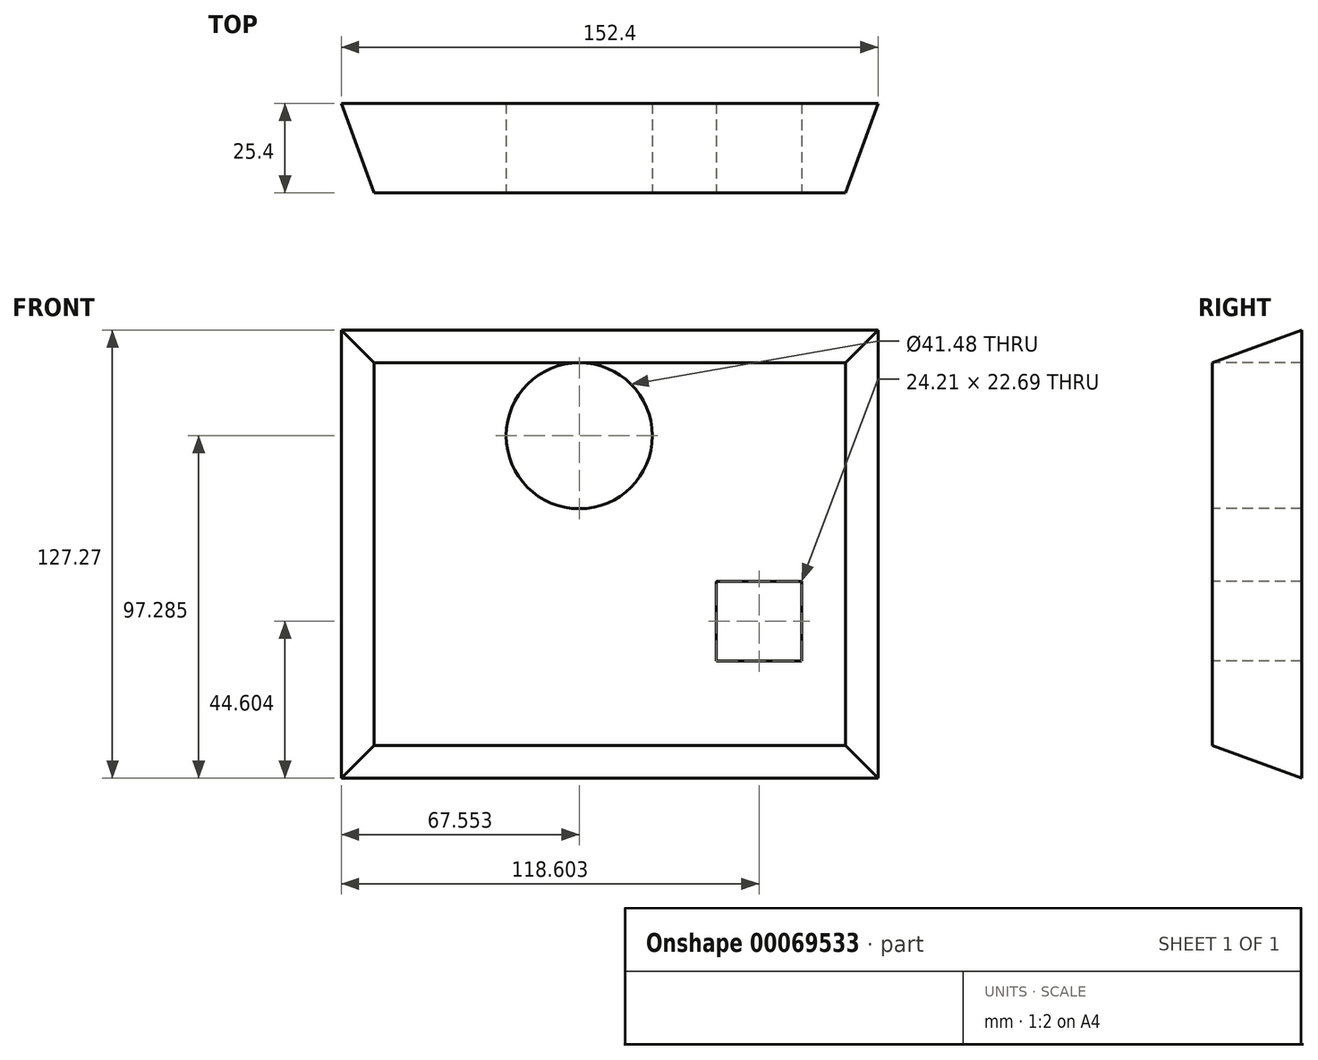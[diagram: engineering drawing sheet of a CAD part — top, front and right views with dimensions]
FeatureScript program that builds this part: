
annotation { "Feature Type Name" : "Feature", "Feature Type Description" : "" }
export const myFeature = defineFeature(function(context is Context, id is Id, definition is map)
    precondition{}
    {
        {
            var Q0;
            Q0=qCreatedBy(makeId("Front.planeOp"),FACE);
            var sketch = newSketch(context, id + "F0", { "sketchPlane" : qUnion([Q0])});
            skLineSegment(sketch, "E0.bottom", {"start": v(0, 0) * mm, "end": v(152.4, 0) * mm});
            skLineSegment(sketch, "E0.top", {"start": v(0, 127.27) * mm, "end": v(152.4, 127.27) * mm});
            skLineSegment(sketch, "E0.left", {"start": v(0, 0) * mm, "end": v(0, 127.27) * mm});
            skLineSegment(sketch, "E0.right", {"start": v(152.4, 0) * mm, "end": v(152.4, 127.27) * mm});
            skSolve(sketch);
        }
        {
            var Q0;
            Q0 = qSketchRegion(id + "F0", true);
            extrude(context, id + "F1", {"entities" : qUnion([Q0]), "depth" : 25.4 * mm, "hasDraft" : true, "draftAngle" : 20 * degree, "draftPullDirection" : true});
        }
        {
            var Q0;
            Q0=makeQuery(id+"F1.opExtrude","CAP_FACE",FACE,{"disambiguationData":[OSD([sQuery(id+"F0.wireOp",EDGE,"E0.bottom"),sQuery(id+"F0.wireOp",EDGE,"E0.top"),sQuery(id+"F0.wireOp",EDGE,"E0.left"),sQuery(id+"F0.wireOp",EDGE,"E0.right")])],"isStart":false});
            var sketch = newSketch(context, id + "F2", { "sketchPlane" : qUnion([Q0])});
            skLineSegment(sketch, "E1.bottom", {"start": v(130.7, 33.26) * mm, "end": v(106.5, 33.26) * mm});
            skLineSegment(sketch, "E1.top", {"start": v(130.7, 55.95) * mm, "end": v(106.5, 55.95) * mm});
            skLineSegment(sketch, "E1.left", {"start": v(130.7, 33.26) * mm, "end": v(130.7, 55.95) * mm});
            skLineSegment(sketch, "E1.right", {"start": v(106.5, 33.26) * mm, "end": v(106.5, 55.95) * mm});
            skSolve(sketch);
        }
        {
            var Q0;
            Q0 = qSketchRegion(id + "F2", true);
            extrude(context, id + "F3", {"entities" : qUnion([Q0]), "operationType" : NewBodyOperationType.REMOVE, "oppositeDirection" : true, "depth" : 25.4 * mm});
        }
        {
            var Q0;
            Q0=makeQuery(id+"F1.opExtrude","CAP_FACE",FACE,{"disambiguationData":[OSD([sQuery(id+"F0.wireOp",EDGE,"E0.bottom"),sQuery(id+"F0.wireOp",EDGE,"E0.top"),sQuery(id+"F0.wireOp",EDGE,"E0.left"),sQuery(id+"F0.wireOp",EDGE,"E0.right")])],"isStart":false});
            var sketch = newSketch(context, id + "F4", { "sketchPlane" : qUnion([Q0])});
            skCircle(sketch, "E2", {"center": v(67.55, 97.28) * mm, "radius": 20.74 * mm});
            skSolve(sketch);
        }
        {
            var Q0;
            Q0 = qSketchRegion(id + "F4", true);
            extrude(context, id + "F5", {"entities" : qUnion([Q0]), "operationType" : NewBodyOperationType.REMOVE, "endBound" : BoundingType.THROUGH_ALL, "oppositeDirection" : true, "depth" : 25.4 * mm});
        }
    });
